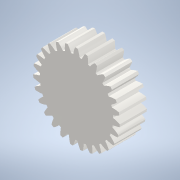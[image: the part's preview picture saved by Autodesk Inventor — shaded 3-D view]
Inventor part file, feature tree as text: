
AUTODESK INVENTOR PART (.ipt)
format: ipt  version: 2022 (Build 260153000, 153)  size: 250,368 bytes
history: native  units: mm (DEFAULTED — no unit token found)
features: plane x3, other x3, sketch x2, extrude x1
ambient origin geometry x8: Origin, YZ Plane, XZ Plane, XY Plane, X Axis, Y Axis, Z Axis, Center Point
bodies: Solid1 (feature_tree)
feature tree (9):
  extrude  "Extrusion1"  Depth=5.0mm TaperAngle=0.0deg
  plane  "Work Plane2"
  plane  "Work Plane8"
  plane  "Work Plane9"
  other  "Spur Gear"
  sketch  "Sketch1"  dims[d0=15.938946mm d1=5.0mm d2=0.0mm]
  sketch  "Sketch2"  dims[d3=14.85mm d4=10.0mm d5=0.0mm d16=15.0mm d17=0.0mm d34=1.163553mm d39=0.0mm d41=0.0mm d43=15.0mm d46=15.0mm d47=0.0mm d48=0.0mm]
  other  "Srf1"
  other  "Pitch Diameter"
